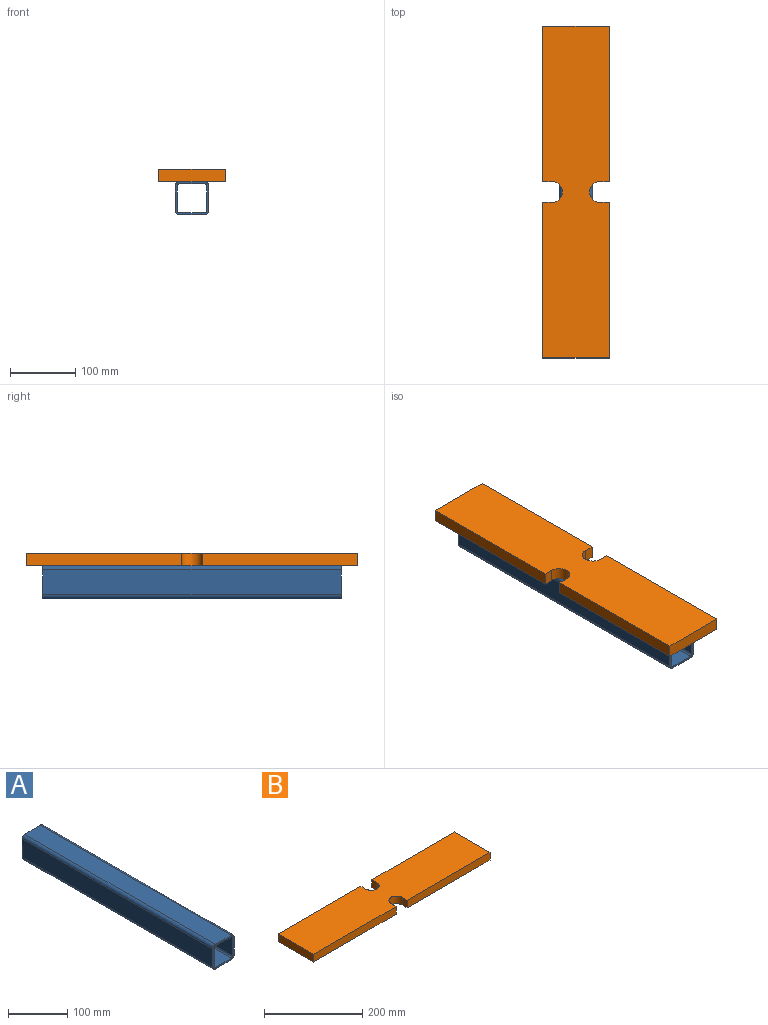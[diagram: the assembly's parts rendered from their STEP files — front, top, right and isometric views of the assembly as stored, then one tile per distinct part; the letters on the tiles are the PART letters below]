
ASSEMBLY  parts=2 mates=1
PART A: 18 faces, bbox 50.8x457.2x50.8 mm
  f0: plane 457.2x38.1mm, normal (0,0,1), area 17419.3mm2, adj f1,f7,f8,f9
  f1: cylinder r=6.35mm len=457.2mm, axis (0,-1,0), area 4560.4mm2, adj f0,f2,f8,f9
  f2: plane 457.2x38.1mm, normal (-1,0,0), area 17419.3mm2, adj f1,f3,f8,f9
  f3: cylinder r=6.35mm len=457.2mm, axis (0,-1,0), area 4560.4mm2, adj f2,f4,f8,f9
  f4: plane 457.2x38.1mm, normal (0,0,-1), area 17419.3mm2, adj f3,f5,f8,f9
  f5: cylinder r=6.35mm len=457.2mm, axis (0,-1,0), area 4560.4mm2, adj f4,f6,f8,f9
  f6: plane 457.2x38.1mm, normal (1,0,0), area 17419.3mm2, adj f5,f7,f8,f9
  f7: cylinder r=6.35mm len=457.2mm, axis (0,-1,0), area 4560.4mm2, adj f0,f6,f8,f9
  f8: plane 50.8x50.8mm, normal (0,1,0), area 578.9mm2, adj f0,f1,f2,f3,f4,f5,f6,f7
  f9: plane 50.8x50.8mm, normal (0,-1,0), area 578.9mm2, adj f0,f1,f2,f3,f4,f5,f6,f7
  f10: cylinder r=3.17mm len=457.2mm, axis (0,-1,0), area 2280.2mm2, adj f8,f9,f11,f17
  f11: plane 457.2x38.1mm, normal (0,0,-1), area 17419.3mm2, adj f8,f9,f10,f12
  f12: cylinder r=3.17mm len=457.2mm, axis (0,-1,0), area 2280.2mm2, adj f8,f9,f11,f13
  f13: plane 457.2x38.1mm, normal (-1,0,0), area 17419.3mm2, adj f8,f9,f12,f14
  f14: cylinder r=3.17mm len=457.2mm, axis (0,-1,0), area 2280.2mm2, adj f8,f9,f13,f15
  f15: plane 457.2x38.1mm, normal (0,0,1), area 17419.3mm2, adj f8,f9,f14,f16
  f16: cylinder r=3.17mm len=457.2mm, axis (0,-1,0), area 2280.2mm2, adj f8,f9,f15,f17
  f17: plane 457.2x38.1mm, normal (1,0,0), area 17419.3mm2, adj f8,f9,f10,f16
PART B: 14 faces, bbox 508x101.6x19.1 mm
  f0: plane 238.13x19.05mm, normal (0,1,0), area 4536.3mm2, adj f2,f6,f7,f13
  f1: plane 238.13x19.05mm, normal (0,-1,0), area 4536.3mm2, adj f2,f6,f7,f8
  f2: plane 508x101.6mm, normal (0,0,1), area 49913.8mm2, adj f0,f1,f3,f4,f5,f6,f8,f9
  f3: plane 238.13x19.05mm, normal (0,1,0), area 4536.3mm2, adj f2,f4,f7,f11
  f4: plane 101.6x19.05mm, normal (-1,0,0), area 1935.5mm2, adj f2,f3,f5,f7
  f5: plane 238.13x19.05mm, normal (0,-1,0), area 4536.3mm2, adj f2,f4,f7,f10
  f6: plane 101.6x19.05mm, normal (1,0,0), area 1935.5mm2, adj f0,f1,f2,f7
  f7: plane 508x101.6mm, normal (0,0,-1), area 49913.8mm2, adj f0,f1,f3,f4,f5,f6,f8,f9
  f8: plane 19.05x14.29mm, normal (-1,0,0), area 272.2mm2, adj f1,f2,f7,f9
  f9: cylinder r=15.88mm len=31.75mm, axis (0,0,1), area 950.1mm2, adj f2,f7,f8,f10
  f10: plane 19.05x14.29mm, normal (1,0,0), area 272.2mm2, adj f2,f5,f7,f9
  f11: plane 19.05x14.29mm, normal (1,0,0), area 272.2mm2, adj f2,f3,f7,f12
  f12: cylinder r=15.88mm len=31.75mm, axis (0,0,1), area 950.1mm2, adj f2,f7,f11,f13
  f13: plane 19.05x14.29mm, normal (-1,0,0), area 272.2mm2, adj f0,f2,f7,f12
PLACE A t=(-109.25,220.96,-102.75)mm
PLACE B rot(axis=(0.71,0.71,0),180deg) t=(-109.25,-7.64,-58.3)mm
MATE fastened B.f2 <-> A.f0  axis (0,0,-1) through (-109.25,-7.64,-77.35)mm
